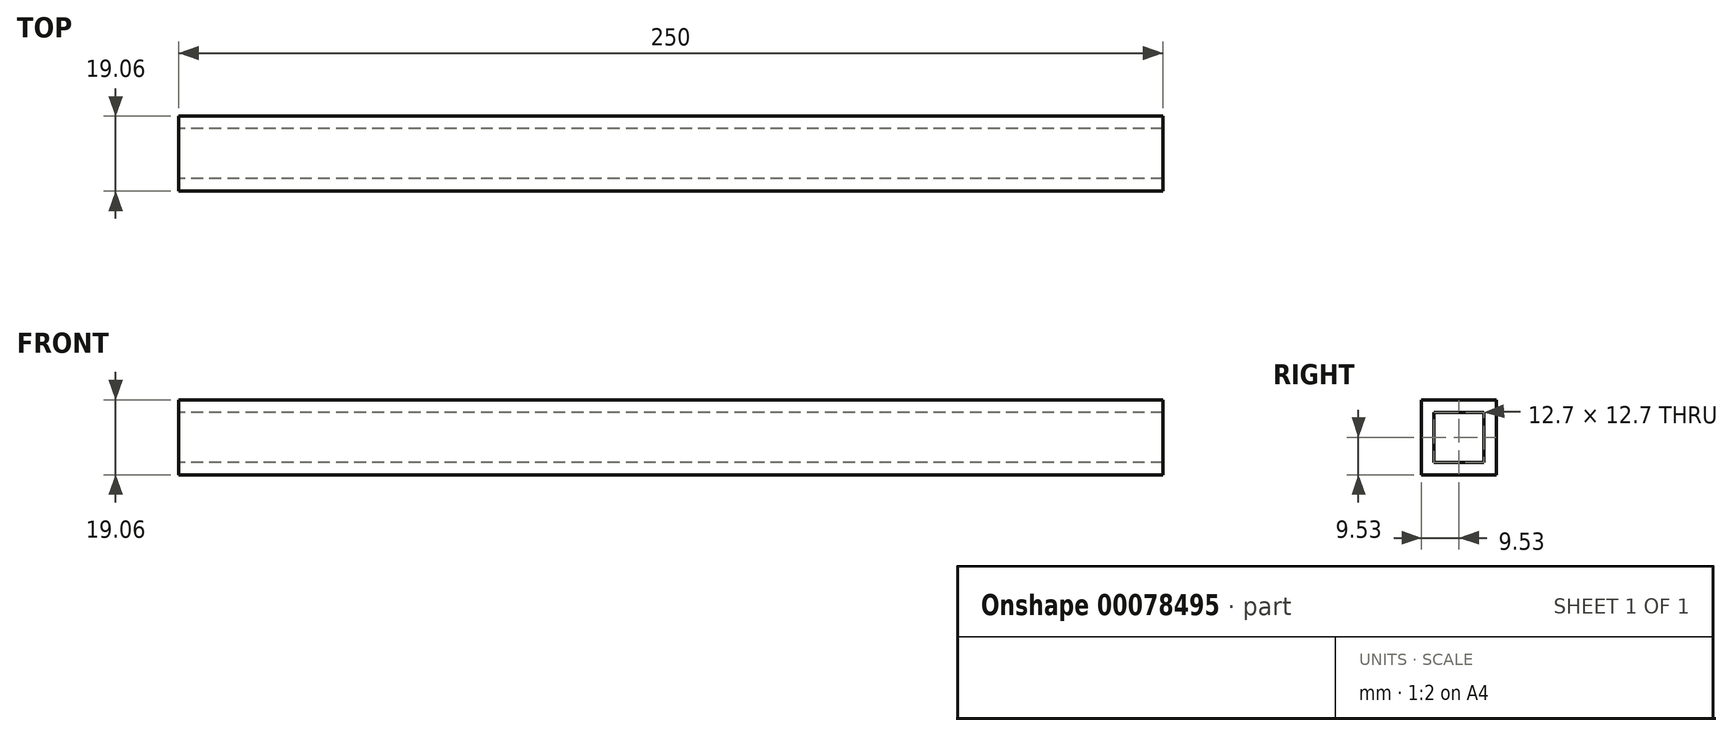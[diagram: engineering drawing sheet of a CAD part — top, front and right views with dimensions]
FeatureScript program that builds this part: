
annotation { "Feature Type Name" : "Feature", "Feature Type Description" : "" }
export const myFeature = defineFeature(function(context is Context, id is Id, definition is map)
    precondition{}
    {
        {
            var Q0;
            Q0=qCreatedBy(makeId("Right.planeOp"),FACE);
            var sketch = newSketch(context, id + "F0", { "sketchPlane" : qUnion([Q0])});
            skLineSegment(sketch, "E0.bottom", {"start": v(9.53, -9.52) * mm, "end": v(-9.53, -9.53) * mm});
            skLineSegment(sketch, "E0.top", {"start": v(9.53, 9.53) * mm, "end": v(-9.53, 9.53) * mm});
            skLineSegment(sketch, "E0.left", {"start": v(9.53, -9.53) * mm, "end": v(9.53, 9.53) * mm});
            skLineSegment(sketch, "E0.right", {"start": v(-9.53, -9.53) * mm, "end": v(-9.53, 9.52) * mm});
            skPoint(sketch, "E0.middle", {"position": v(0, 0) * mm});
            skLineSegment(sketch, "E1.bottom", {"start": v(6.35, -6.35) * mm, "end": v(-6.35, -6.35) * mm});
            skLineSegment(sketch, "E1.top", {"start": v(6.35, 6.35) * mm, "end": v(-6.35, 6.35) * mm});
            skLineSegment(sketch, "E1.left", {"start": v(6.35, -6.35) * mm, "end": v(6.35, 6.35) * mm});
            skLineSegment(sketch, "E1.right", {"start": v(-6.35, -6.35) * mm, "end": v(-6.35, 6.35) * mm});
            skSolve(sketch);
        }
        {
            var Q0;
            Q0 = qSketchRegion(id + "F0", true);
            extrude(context, id + "F1", {"entities" : qUnion([Q0]), "endBound" : BoundingType.SYMMETRIC, "depth" : 250 * mm});
        }
    });
